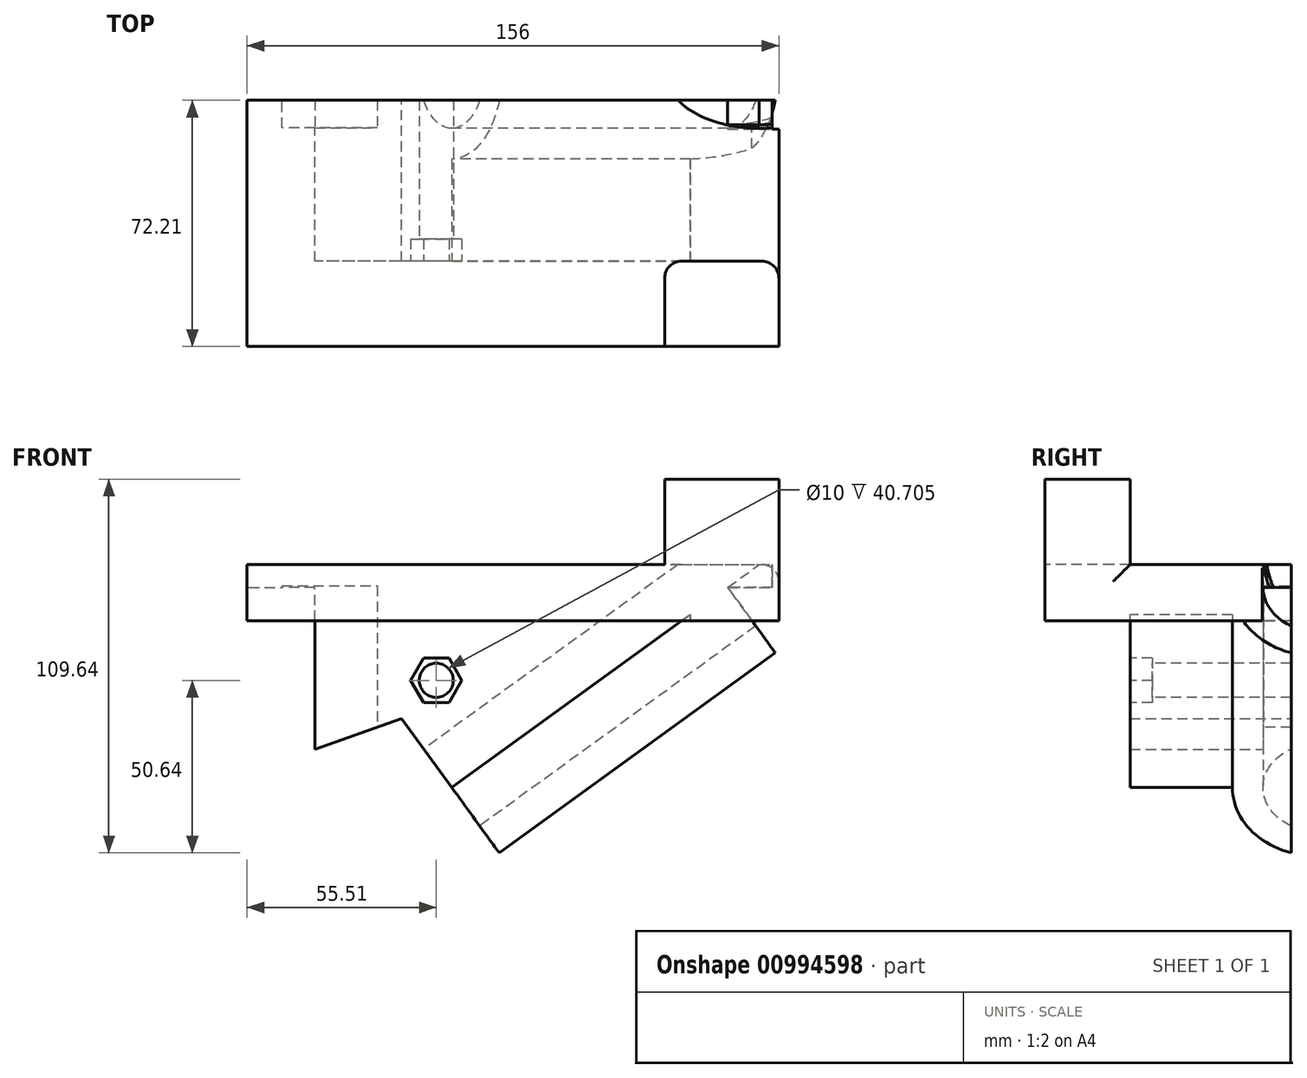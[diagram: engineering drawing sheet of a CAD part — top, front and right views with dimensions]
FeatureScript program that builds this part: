
annotation { "Feature Type Name" : "Feature", "Feature Type Description" : "" }
export const myFeature = defineFeature(function(context is Context, id is Id, definition is map)
    precondition{}
    {
        {
            var Q0;
            Q0=qCreatedBy(makeId("Front.planeOp"),FACE);
            var sketch = newSketch(context, id + "F0", { "sketchPlane" : qUnion([Q0])});
            skLineSegment(sketch, "E0.bottom", {"start": v(65.5, 0) * mm, "end": v(-65.5, 0) * mm});
            skLineSegment(sketch, "E0.top", {"start": v(65.5, 155.25) * mm, "end": v(-65.5, 155.25) * mm});
            skLineSegment(sketch, "E0.left", {"start": v(65.5, 0) * mm, "end": v(65.5, 155.25) * mm});
            skLineSegment(sketch, "E0.right", {"start": v(-65.5, 0) * mm, "end": v(-65.5, 155.25) * mm});
            skLineSegment(sketch, "E1.bottom", {"start": v(-65.5, 0) * mm, "end": v(89.5, 0) * mm});
            skLineSegment(sketch, "E1.top", {"start": v(-65.5, -12.7) * mm, "end": v(89.5, -12.7) * mm});
            skLineSegment(sketch, "E1.left", {"start": v(-65.5, 0) * mm, "end": v(-65.5, -12.7) * mm});
            skLineSegment(sketch, "E1.right", {"start": v(89.5, 0) * mm, "end": v(89.5, -12.7) * mm});
            skCircle(sketch, "E2", {"center": v(-32.75, 57) * mm, "radius": 5 * mm});
            skCircle(sketch, "E3.0.1.0", {"center": v(-32.75, 122.5) * mm, "radius": 5 * mm});
            skCircle(sketch, "E3.1.0.0", {"center": v(32.75, 57) * mm, "radius": 5 * mm});
            skCircle(sketch, "E3.1.1.0", {"center": v(32.75, 122.5) * mm, "radius": 5 * mm});
            skLineSegment(sketch, "E3.direction1", {"start": v(-32.75, 57) * mm, "end": v(32.75, 57) * mm, "construction": true});
            skLineSegment(sketch, "E3.direction2", {"start": v(-32.75, 57) * mm, "end": v(-32.75, 122.5) * mm, "construction": true});
            skCircle(sketch, "E4", {"center": v(0, 89.75) * mm, "radius": 10 * mm});
            skSolve(sketch);
        }
        {
            var Q0;
            Q0=makeQuery(id+"F0.imprint","IMPRINT",FACE,{"disambiguationData":[TD([[makeQuery(id+"F0.imprint","IMPRINT",EDGE,{"derivedFrom":sQuery(id+"F0.wireOp",EDGE,"E0.top")}),1.0]])]});
            extrude(context, id + "F1", {"entities" : qUnion([Q0]), "oppositeDirection" : true, "depth" : 12.7 * mm, "offsetDistance" : 25 * mm});
        }
        {
            var Q0;
            Q0=makeQuery(id+"F0.imprint","IMPRINT",FACE,{"disambiguationData":[TD([[makeQuery(id+"F0.imprint","IMPRINT",EDGE,{"derivedFrom":sQuery(id+"F0.wireOp",EDGE,"E1.bottom")}),-1.0]])]});
            extrude(context, id + "F2", {"entities" : qUnion([Q0]), "operationType" : NewBodyOperationType.ADD, "oppositeDirection" : true, "depth" : 150 * mm, "offsetDistance" : 25 * mm});
        }
        {
            var Q0;
            Q0=makeQuery(id+"F2.opExtrude","SWEPT_FACE",FACE,{"disambiguationData":[OSD([sQuery(id+"F0.wireOp",EDGE,"E1.top")])]});
            var sketch = newSketch(context, id + "F3", { "sketchPlane" : qUnion([Q0])});
            skLineSegment(sketch, "E5", {"start": v(89.5, -12.7) * mm, "end": v(-65.5, -12.7) * mm});
            skCircle(sketch, "E6", {"center": v(-40, -55.7) * mm, "radius": 4.76 * mm});
            skCircle(sketch, "E7.0.1.0", {"center": v(-40, -118.2) * mm, "radius": 4.76 * mm});
            skCircle(sketch, "E7.1.0.0", {"center": v(64, -55.7) * mm, "radius": 4.76 * mm});
            skCircle(sketch, "E7.1.1.0", {"center": v(64, -118.2) * mm, "radius": 4.76 * mm});
            skLineSegment(sketch, "E7.direction1", {"start": v(-40, -55.7) * mm, "end": v(64, -55.7) * mm, "construction": true});
            skLineSegment(sketch, "E7.direction2", {"start": v(-40, -55.7) * mm, "end": v(-40, -118.2) * mm, "construction": true});
            skSolve(sketch);
        }
        {
            var Q0;
            Q0=makeQuery(id+"F3.imprint","IMPRINT",FACE,{"disambiguationData":[TD([[makeQuery(id+"F3.imprint","IMPRINT",EDGE,{"derivedFrom":sQuery(id+"F3.wireOp",EDGE,"E6")}),1.0]])]});
            var Q1;
            Q1=makeQuery(id+"F3.imprint","IMPRINT",FACE,{"disambiguationData":[TD([[makeQuery(id+"F3.imprint","IMPRINT",EDGE,{"derivedFrom":sQuery(id+"F3.wireOp",EDGE,"E7.0.1.0")}),1.0]])]});
            var Q2;
            Q2=makeQuery(id+"F3.imprint","IMPRINT",FACE,{"disambiguationData":[TD([[makeQuery(id+"F3.imprint","IMPRINT",EDGE,{"derivedFrom":sQuery(id+"F3.wireOp",EDGE,"E7.1.1.0")}),1.0]])]});
            var Q3;
            Q3=makeQuery(id+"F3.imprint","IMPRINT",FACE,{"disambiguationData":[TD([[makeQuery(id+"F3.imprint","IMPRINT",EDGE,{"derivedFrom":sQuery(id+"F3.wireOp",EDGE,"E7.1.0.0")}),1.0]])]});
            extrude(context, id + "F4", {"entities" : qUnion([Q0, Q1, Q2, Q3]), "operationType" : NewBodyOperationType.REMOVE, "endBound" : BoundingType.THROUGH_ALL, "oppositeDirection" : true, "depth" : 25 * mm, "offsetDistance" : 25 * mm});
        }
        {
            var Q0;
            {var subQ0=sQuery(id+"F0.wireOp",EDGE,"E1.bottom");Q0=makeQuery(id+"F2.boolean.opBoolean","MERGE",FACE,{"derivedFrom":[makeQuery(id+"F1.opExtrude","CAP_FACE",FACE,{"disambiguationData":[OSD([sQuery(id+"F0.wireOp",EDGE,"E0.top"),sQuery(id+"F0.wireOp",EDGE,"E0.left"),sQuery(id+"F0.wireOp",EDGE,"E0.right"),subQ0,sQuery(id+"F0.wireOp",EDGE,"E2"),sQuery(id+"F0.wireOp",EDGE,"E3.0.1.0"),sQuery(id+"F0.wireOp",EDGE,"E3.1.0.0"),sQuery(id+"F0.wireOp",EDGE,"E3.1.1.0"),sQuery(id+"F0.wireOp",EDGE,"E4")])],"isStart":true}),makeQuery(id+"F2.opExtrude","CAP_FACE",FACE,{"disambiguationData":[OSD([subQ0,sQuery(id+"F0.wireOp",EDGE,"E1.top"),sQuery(id+"F0.wireOp",EDGE,"E1.left"),sQuery(id+"F0.wireOp",EDGE,"E1.right")])],"isStart":true})]});}
            var sketch = newSketch(context, id + "F5", { "sketchPlane" : qUnion([Q0])});
            skLineSegment(sketch, "E8", {"start": v(-63.5, -12.7) * mm, "end": v(-44.93, -100.76) * mm});
            skLineSegment(sketch, "E9", {"start": v(-44.93, -100.76) * mm, "end": v(76.5, -12.7) * mm});
            skSolve(sketch);
        }
        {
            var Q0;
            {var subQ0=sQuery(id+"F5.wireOp",EDGE,"E8");Q0=makeQuery(id+"F5.imprint","IMPRINT",FACE,{"disambiguationData":[TD([[makeQuery(id+"F5.imprint","IMPRINT",EDGE,{"derivedFrom":subQ0}),1.0]])]});}
            extrude(context, id + "F6", {"entities" : qUnion([Q0]), "operationType" : NewBodyOperationType.ADD, "oppositeDirection" : true, "depth" : 55 * mm, "offsetDistance" : 25 * mm});
        }
        {
            var Q0;
            Q0=makeQuery(id+"F6.opExtrude","SWEPT_FACE",FACE,{"disambiguationData":[OSD([sQuery(id+"F5.wireOp",EDGE,"E9")])]});
            var sketch = newSketch(context, id + "F7", { "sketchPlane" : qUnion([Q0])});
            skLineSegment(sketch, "E10", {"start": v(54.47, -55) * mm, "end": v(-45.53, -55) * mm});
            skLineSegment(sketch, "E11", {"start": v(-45.53, -55) * mm, "end": v(-45.53, -30) * mm});
            skLineSegment(sketch, "E12", {"start": v(-45.53, -30) * mm, "end": v(54.47, -30) * mm});
            skLineSegment(sketch, "E13", {"start": v(54.47, -30) * mm, "end": v(54.47, -55) * mm});
            skLineSegment(sketch, "E14", {"start": v(-45.53, -40) * mm, "end": v(18.27, -40) * mm});
            skLineSegment(sketch, "E15", {"start": v(18.27, -40) * mm, "end": v(54.47, -40) * mm});
            skSolve(sketch);
        }
        {
            var Q0;
            {var subQ2=sQuery(id+"F7.wireOp",EDGE,"E12");Q0=makeQuery(id+"F7.imprint","IMPRINT",FACE,{"disambiguationData":[TD([[makeQuery(id+"F7.imprint","IMPRINT",EDGE,{"derivedFrom":subQ2}),-1.0]])]});}
            var Q1;
            Q1=sQuery(id+"F7.wireOp",EDGE,"E10");
            revolve(context, id + "F8", {"operationType" : NewBodyOperationType.ADD, "surfaceOperationType" : NewSurfaceOperationType.NEW, "entities" : qUnion([Q0]), "axis" : qUnion([Q1]), "revolveType" : RevolveType.FULL, "oppositeDirection" : true});
        }
        {
            var Q0;
            Q0=makeQuery(id+"F2.opExtrude","SWEPT_FACE",FACE,{"disambiguationData":[OSD([sQuery(id+"F0.wireOp",EDGE,"E1.right")])]});
            var sketch = newSketch(context, id + "F9", { "sketchPlane" : qUnion([Q0])});
            skLineSegment(sketch, "E16.bottom", {"start": v(34.14, 0) * mm, "end": v(80.6, 0) * mm});
            skLineSegment(sketch, "E16.top", {"start": v(34.14, 23.6) * mm, "end": v(80.6, 23.6) * mm});
            skLineSegment(sketch, "E16.left", {"start": v(34.14, 0) * mm, "end": v(34.14, 23.6) * mm});
            skLineSegment(sketch, "E16.right", {"start": v(80.6, 0) * mm, "end": v(80.6, 23.6) * mm});
            skSolve(sketch);
        }
        {
            var Q0;
            Q0=makeQuery(id+"F9.imprint","IMPRINT",FACE,{"disambiguationData":[TD([[makeQuery(id+"F9.imprint","IMPRINT",EDGE,{"derivedFrom":sQuery(id+"F9.wireOp",EDGE,"E16.bottom")}),-1.0]])]});
            extrude(context, id + "F10", {"entities" : qUnion([Q0]), "operationType" : NewBodyOperationType.REMOVE, "oppositeDirection" : true, "depth" : 100.62 * mm, "offsetDistance" : 25 * mm});
        }
        {
            var Q0;
            Q0=qCreatedBy(makeId("Front.planeOp"),FACE);
            var sketch = newSketch(context, id + "F11", { "sketchPlane" : qUnion([Q0])});
            skLineSegment(sketch, "E17.bottom", {"start": v(-4.59, -72.84) * mm, "end": v(-55.62, -72.84) * mm});
            skLineSegment(sketch, "E17.top", {"start": v(-4.59, -104.11) * mm, "end": v(-55.62, -104.11) * mm});
            skLineSegment(sketch, "E17.left", {"start": v(-4.59, -72.84) * mm, "end": v(-4.59, -104.11) * mm});
            skLineSegment(sketch, "E17.right", {"start": v(-55.62, -72.84) * mm, "end": v(-55.62, -104.11) * mm});
            skLineSegment(sketch, "E18.bottom", {"start": v(-63.9, -12.7) * mm, "end": v(-44.63, -12.7) * mm});
            skLineSegment(sketch, "E18.top", {"start": v(-63.9, -72.84) * mm, "end": v(-44.63, -72.84) * mm});
            skLineSegment(sketch, "E18.left", {"start": v(-63.9, -12.7) * mm, "end": v(-63.9, -72.84) * mm});
            skLineSegment(sketch, "E18.right", {"start": v(-44.63, -12.7) * mm, "end": v(-44.63, -72.84) * mm});
            skSolve(sketch);
        }
        {
            var Q0;
            Q0=makeQuery(id+"F11.imprint","IMPRINT",FACE,{"disambiguationData":[TD([[makeQuery(id+"F11.imprint","IMPRINT",EDGE,{"derivedFrom":sQuery(id+"F11.wireOp",EDGE,"E18.bottom")}),-1.0]])]});
            var Q1;
            {var subQ1=sQuery(id+"F11.wireOp",EDGE,"E17.bottom");Q1=makeQuery(id+"F11.imprint","IMPRINT",FACE,{"disambiguationData":[TD([[makeQuery(id+"F11.imprint","IMPRINT",EDGE,{"derivedFrom":subQ1}),1.0]])]});}
            extrude(context, id + "F12", {"entities" : qUnion([Q0, Q1]), "operationType" : NewBodyOperationType.REMOVE, "endBound" : BoundingType.THROUGH_ALL, "oppositeDirection" : true, "depth" : 63.06 * mm, "offsetDistance" : 25 * mm});
        }
        {
            var Q0;
            Q0=makeQuery(id+"F6.opExtrude","CAP_FACE",FACE,{"disambiguationData":[OSD([sQuery(id+"F0.wireOp",EDGE,"E1.top"),sQuery(id+"F5.wireOp",EDGE,"E8"),sQuery(id+"F5.wireOp",EDGE,"E9")])],"isStart":false});
            var sketch = newSketch(context, id + "F13", { "sketchPlane" : qUnion([Q0])});
            skLineSegment(sketch, "E19", {"start": v(19.13, -51.17) * mm, "end": v(-10.05, -91.4) * mm});
            skLineSegment(sketch, "E20", {"start": v(-10.05, -91.4) * mm, "end": v(37.2, -125.68) * mm});
            skLineSegment(sketch, "E21", {"start": v(37.2, -125.68) * mm, "end": v(76.4, -71.65) * mm});
            skLineSegment(sketch, "E22", {"start": v(76.4, -71.65) * mm, "end": v(19.13, -51.17) * mm});
            skSolve(sketch);
        }
        {
            var Q0;
            {var subQ10=sQuery(id+"F13.wireOp",EDGE,"E20");Q0=makeQuery(id+"F13.imprint","IMPRINT",FACE,{"disambiguationData":[TD([[makeQuery(id+"F13.imprint","IMPRINT",EDGE,{"derivedFrom":subQ10}),1.0]])]});}
            var Q1;
            {var subQ0=sQuery(id+"F5.wireOp",EDGE,"E9");var subQ1=makeQuery(id+"F6.opExtrude","CAP_FACE",FACE,{"disambiguationData":[OSD([sQuery(id+"F0.wireOp",EDGE,"E1.top"),sQuery(id+"F5.wireOp",EDGE,"E8"),subQ0])],"isStart":false});var subQ2=subQ1;var subQ3=makeQuery(id+"F12.boolean.opBoolean","INTERSECT",EDGE,{"derivedFrom":[subQ2,makeQuery(id+"F12.opExtrude","SWEPT_FACE",FACE,{"disambiguationData":[OSD([sQuery(id+"F11.wireOp",EDGE,"E17.bottom")])]})]});Q1=makeQuery(id+"F13.imprint","IMPRINT",FACE,{"disambiguationData":[TD([[makeQuery(id+"F13.imprint","IMPRINT",EDGE,{"derivedFrom":subQ3}),1.0]])]});}
            extrude(context, id + "F14", {"entities" : qUnion([Q0, Q1]), "operationType" : NewBodyOperationType.REMOVE, "oppositeDirection" : true, "depth" : 89 * mm, "offsetDistance" : 25 * mm});
        }
        {
            var Q0;
            Q0=makeQuery(id+"F14.boolean.opBoolean","MERGE",FACE,{"derivedFrom":[makeQuery(id+"F8.opRevolve","SWEPT_FACE",FACE,{"disambiguationData":[OSD([sQuery(id+"F7.wireOp",EDGE,"E11")])]})],"fromTools":[makeQuery(id+"F14.opExtrude","SWEPT_FACE",FACE,{"disambiguationData":[OSD([sQuery(id+"F13.wireOp",EDGE,"E19")])]})]});
            var sketch = newSketch(context, id + "F15", { "sketchPlane" : qUnion([Q0])});
            skCircle(sketch, "E23", {"center": v(-55, -55.2) * mm, "radius": 16 * mm});
            skSolve(sketch);
        }
        {
            var Q0;
            {var subQ0=sQuery(id+"F13.wireOp",EDGE,"E19");Q0=makeQuery(id+"F15.imprint","IMPRINT",FACE,{"disambiguationData":[TD([[makeQuery(id+"F15.imprint","IMPRINT",EDGE,{"derivedFrom":makeQuery(id+"F14.boolean.opBoolean","COPY",EDGE,{"derivedFrom":makeQuery(id+"F14.opExtrude","CAP_EDGE",EDGE,{"disambiguationData":[OSD([subQ0])],"isStart":true})})}),-1.0]])]});}
            var Q1;
            Q1=makeQuery(id+"F15.imprint","IMPRINT",FACE,{"disambiguationData":[TD([[makeQuery(id+"F15.imprint","IMPRINT",EDGE,{"derivedFrom":sQuery(id+"F15.wireOp",EDGE,"E23")}),1.0]])]});
            extrude(context, id + "F16", {"entities" : qUnion([Q0, Q1]), "operationType" : NewBodyOperationType.REMOVE, "endBound" : BoundingType.THROUGH_ALL, "oppositeDirection" : true, "depth" : 25 * mm, "offsetDistance" : 25 * mm});
        }
        {
            var Q0;
            {var subQ1=sQuery(id+"F0.wireOp",EDGE,"E1.right");var subQ3=sQuery(id+"F0.wireOp",EDGE,"E1.top");var subQ6=makeQuery(id+"F2.opExtrude","SWEPT_FACE",FACE,{"disambiguationData":[OSD([subQ3])]});var subQ14=makeQuery(id+"F2.opExtrude","SWEPT_FACE",FACE,{"disambiguationData":[OSD([subQ1])]});var subQ17=makeQuery(id+"F4.boolean.opBoolean","COPY",FACE,{"derivedFrom":makeQuery(id+"F4.opExtrude","SWEPT_FACE",FACE,{"disambiguationData":[OSD([sQuery(id+"F3.wireOp",EDGE,"E6")])]})});Q0=makeQuery(id+"F16.boolean.opBoolean","SPLIT",FACE,{"disambiguationData":[TD([subQ17])],"derivedFrom":makeQuery(id+"F12.boolean.opBoolean","SPLIT",FACE,{"disambiguationData":[TD([subQ14])],"derivedFrom":subQ6})});}
            cPlane(context, id + "F17", {"entities" : qUnion([Q0]), "cplaneType" : CPlaneType.OFFSET, "offset" : 57.01 * mm, "width" : 150 * mm, "height" : 150 * mm});
        }
        {
            var Q0;
            Q0=qCreatedBy(id+"F17.planeOp",FACE);
            var sketch = newSketch(context, id + "F18", { "sketchPlane" : qUnion([Q0])});
            skLineSegment(sketch, "E24.bottom", {"start": v(-26.24, -39.17) * mm, "end": v(-54.25, -39.17) * mm});
            skLineSegment(sketch, "E24.top", {"start": v(-26.24, -72.55) * mm, "end": v(-54.25, -72.55) * mm});
            skLineSegment(sketch, "E24.left", {"start": v(-26.24, -39.17) * mm, "end": v(-26.24, -72.55) * mm});
            skLineSegment(sketch, "E24.right", {"start": v(-54.25, -39.17) * mm, "end": v(-54.25, -72.55) * mm});
            skSolve(sketch);
        }
        {
            var Q0;
            Q0=makeQuery(id+"F18.imprint","IMPRINT",FACE,{"disambiguationData":[TD([[makeQuery(id+"F18.imprint","IMPRINT",EDGE,{"derivedFrom":sQuery(id+"F18.wireOp",EDGE,"E24.bottom")}),1.0]])]});
            extrude(context, id + "F19", {"entities" : qUnion([Q0]), "operationType" : NewBodyOperationType.REMOVE, "oppositeDirection" : true, "depth" : 57.44 * mm, "offsetDistance" : 25 * mm});
        }
        {
            var Q0;
            {var subQ1=sQuery(id+"F0.wireOp",EDGE,"E1.right");var subQ3=sQuery(id+"F0.wireOp",EDGE,"E1.top");var subQ6=makeQuery(id+"F2.opExtrude","SWEPT_FACE",FACE,{"disambiguationData":[OSD([subQ3])]});var subQ14=makeQuery(id+"F2.opExtrude","SWEPT_FACE",FACE,{"disambiguationData":[OSD([subQ1])]});var subQ17=makeQuery(id+"F4.boolean.opBoolean","COPY",FACE,{"derivedFrom":makeQuery(id+"F4.opExtrude","SWEPT_FACE",FACE,{"disambiguationData":[OSD([sQuery(id+"F3.wireOp",EDGE,"E6")])]})});Q0=makeQuery(id+"F16.boolean.opBoolean","SPLIT",FACE,{"disambiguationData":[TD([subQ17])],"derivedFrom":makeQuery(id+"F12.boolean.opBoolean","SPLIT",FACE,{"disambiguationData":[TD([subQ14])],"derivedFrom":subQ6})});}
            cPlane(context, id + "F20", {"entities" : qUnion([Q0]), "cplaneType" : CPlaneType.OFFSET, "offset" : 94.9 * mm, "width" : 150 * mm, "height" : 150 * mm});
        }
        {
            var Q0;
            Q0=makeQuery(id+"F2.opExtrude","CAP_FACE",FACE,{"disambiguationData":[OSD([sQuery(id+"F0.wireOp",EDGE,"E1.bottom"),sQuery(id+"F0.wireOp",EDGE,"E1.top"),sQuery(id+"F0.wireOp",EDGE,"E1.left"),sQuery(id+"F0.wireOp",EDGE,"E1.right")])],"isStart":false});
            cPlane(context, id + "F21", {"entities" : qUnion([Q0]), "cplaneType" : CPlaneType.OFFSET, "offset" : 83.64 * mm, "oppositeDirection" : true, "width" : 150 * mm, "height" : 150 * mm});
        }
        {
            var Q0;
            Q0=qCreatedBy(id+"F21.planeOp",FACE);
            var sketch = newSketch(context, id + "F22", { "sketchPlane" : qUnion([Q0])});
            skLineSegment(sketch, "E25.bottom", {"start": v(-19.5, -47.14) * mm, "end": v(25.5, -47.14) * mm});
            skLineSegment(sketch, "E25.top", {"start": v(-19.5, -10.84) * mm, "end": v(25.5, -10.84) * mm});
            skLineSegment(sketch, "E25.left", {"start": v(-19.5, -47.14) * mm, "end": v(-19.5, -10.84) * mm});
            skLineSegment(sketch, "E25.right", {"start": v(25.5, -47.14) * mm, "end": v(25.5, -10.84) * mm});
            skLineSegment(sketch, "E26", {"start": v(9.29, -47.14) * mm, "end": v(-19.5, -25.37) * mm});
            skSolve(sketch);
        }
        {
            var Q0;
            {var subQ2=sQuery(id+"F22.wireOp",EDGE,"E25.top");Q0=makeQuery(id+"F22.imprint","IMPRINT",FACE,{"disambiguationData":[TD([[makeQuery(id+"F22.imprint","IMPRINT",EDGE,{"derivedFrom":subQ2}),-1.0]])]});}
            extrude(context, id + "F23", {"entities" : qUnion([Q0]), "operationType" : NewBodyOperationType.ADD, "oppositeDirection" : true, "depth" : 37.3 * mm, "offsetDistance" : 25 * mm});
        }
        {
            var Q0;
            Q0=qCreatedBy(id+"F20.planeOp",FACE);
            var sketch = newSketch(context, id + "F24", { "sketchPlane" : qUnion([Q0])});
            skLineSegment(sketch, "E27", {"start": v(-70.25, -47.2) * mm, "end": v(105.05, -47.2) * mm});
            skLineSegment(sketch, "E28", {"start": v(105.05, -47.2) * mm, "end": v(105.05, 16.74) * mm});
            skLineSegment(sketch, "E29", {"start": v(105.05, 16.74) * mm, "end": v(-70.14, 16.74) * mm});
            skLineSegment(sketch, "E30", {"start": v(-70.14, 16.74) * mm, "end": v(-70.25, -47.2) * mm});
            skLineSegment(sketch, "E31", {"start": v(-70.25, -47.2) * mm, "end": v(-70.25, -164.49) * mm});
            skLineSegment(sketch, "E32", {"start": v(-70.25, -164.49) * mm, "end": v(108.53, -164.49) * mm});
            skLineSegment(sketch, "E33", {"start": v(108.53, -164.49) * mm, "end": v(105.05, -47.2) * mm});
            skSolve(sketch);
        }
        {
            var Q0;
            Q0=makeQuery(id+"F24.imprint","IMPRINT",FACE,{"disambiguationData":[TD([[makeQuery(id+"F24.imprint","IMPRINT",EDGE,{"derivedFrom":sQuery(id+"F24.wireOp",EDGE,"E27")}),-1.0]])]});
            extrude(context, id + "F25", {"entities" : qUnion([Q0]), "operationType" : NewBodyOperationType.REMOVE, "endBound" : BoundingType.THROUGH_ALL, "oppositeDirection" : true, "depth" : 25 * mm, "offsetDistance" : 25 * mm});
        }
        {
            var Q0;
            Q0=qCreatedBy(makeId("Front.planeOp"),FACE);
            var sketch = newSketch(context, id + "F26", { "sketchPlane" : qUnion([Q0])});
            skLineSegment(sketch, "E34.bottom", {"start": v(65.5, 10.5) * mm, "end": v(-64.5, 10.5) * mm});
            skLineSegment(sketch, "E34.top", {"start": v(65.5, -22.5) * mm, "end": v(-64.5, -22.5) * mm});
            skLineSegment(sketch, "E34.left", {"start": v(65.5, 10.5) * mm, "end": v(65.5, -22.5) * mm});
            skLineSegment(sketch, "E34.right", {"start": v(-64.5, 10.5) * mm, "end": v(-64.5, -22.5) * mm});
            skSolve(sketch);
        }
        {
            var Q0;
            Q0=makeQuery(id+"F26.imprint","IMPRINT",FACE,{"disambiguationData":[TD([[makeQuery(id+"F26.imprint","IMPRINT",EDGE,{"derivedFrom":sQuery(id+"F26.wireOp",EDGE,"E34.bottom")}),1.0]])]});
            extrude(context, id + "F27", {"entities" : qUnion([Q0]), "operationType" : NewBodyOperationType.ADD, "depth" : 25 * mm, "offsetDistance" : 25 * mm});
        }
        {
            var Q0;
            {var subQ2=sQuery(id+"F0.wireOp",EDGE,"E1.top");var subQ8=sQuery(id+"F26.wireOp",EDGE,"E34.top");var subQ9=sQuery(id+"F26.wireOp",EDGE,"E34.right");Q0=makeQuery(id+"F27.boolean.opBoolean","SPLIT",FACE,{"disambiguationData":[TD([makeQuery(id+"F2.opExtrude","SWEPT_FACE",FACE,{"disambiguationData":[OSD([subQ2])]})])],"derivedFrom":makeQuery(id+"F27.opExtrude","CAP_FACE",FACE,{"disambiguationData":[OSD([sQuery(id+"F26.wireOp",EDGE,"E34.bottom"),subQ8,sQuery(id+"F26.wireOp",EDGE,"E34.left"),subQ9])],"isStart":true})});}
            extrude(context, id + "F28", {"entities" : qUnion([Q0]), "operationType" : NewBodyOperationType.ADD, "depth" : 47.17 * mm, "offsetDistance" : 25 * mm});
        }
        {
            var Q0;
            Q0=makeQuery(id+"F27.opExtrude","CAP_FACE",FACE,{"disambiguationData":[OSD([sQuery(id+"F26.wireOp",EDGE,"E34.bottom"),sQuery(id+"F26.wireOp",EDGE,"E34.top"),sQuery(id+"F26.wireOp",EDGE,"E34.left"),sQuery(id+"F26.wireOp",EDGE,"E34.right")])],"isStart":false});
            var sketch = newSketch(context, id + "F29", { "sketchPlane" : qUnion([Q0])});
            skLineSegment(sketch, "E35", {"start": v(102.44, -6) * mm, "end": v(-95.08, -6) * mm});
            skLineSegment(sketch, "E36", {"start": v(102.44, -6) * mm, "end": v(102.44, -90.83) * mm});
            skLineSegment(sketch, "E37", {"start": v(102.44, -90.83) * mm, "end": v(-96.5, -90.83) * mm});
            skLineSegment(sketch, "E38", {"start": v(-96.5, -90.83) * mm, "end": v(-95.08, -6) * mm});
            skLineSegment(sketch, "E39", {"start": v(-95.08, -6) * mm, "end": v(-95.08, 171.2) * mm});
            skLineSegment(sketch, "E40", {"start": v(-95.08, 171.2) * mm, "end": v(114.36, 171.2) * mm});
            skLineSegment(sketch, "E41", {"start": v(114.36, 171.2) * mm, "end": v(102.44, -6) * mm});
            skSolve(sketch);
        }
        {
            var Q0;
            {var subQ0=sQuery(id+"F29.wireOp",EDGE,"E39");Q0=makeQuery(id+"F29.imprint","IMPRINT",FACE,{"disambiguationData":[TD([[makeQuery(id+"F29.imprint","IMPRINT",EDGE,{"derivedFrom":subQ0}),-1.0]])]});}
            var Q1;
            {var subQ5=makeQuery(id+"F27.opExtrude","CAP_EDGE",EDGE,{"disambiguationData":[OSD([sQuery(id+"F26.wireOp",EDGE,"E34.bottom")])],"isStart":false});Q1=makeQuery(id+"F29.imprint","IMPRINT",FACE,{"disambiguationData":[TD([[makeQuery(id+"F29.imprint","IMPRINT",EDGE,{"derivedFrom":subQ5}),1.0]])]});}
            extrude(context, id + "F30", {"entities" : qUnion([Q0, Q1]), "operationType" : NewBodyOperationType.REMOVE, "oppositeDirection" : true, "depth" : 118.07 * mm, "offsetDistance" : 25 * mm});
        }
        {
            var Q0;
            {var subQ0=sQuery(id+"F5.wireOp",EDGE,"E9");var subQ1=sQuery(id+"F5.wireOp",EDGE,"E8");var subQ2=sQuery(id+"F0.wireOp",EDGE,"E1.top");var subQ3=makeQuery(id+"F6.opExtrude","CAP_FACE",FACE,{"disambiguationData":[OSD([subQ2,subQ1,subQ0])],"isStart":true});var subQ4=sQuery(id+"F0.wireOp",EDGE,"E1.bottom");var subQ5=makeQuery(id+"F2.opExtrude","CAP_FACE",FACE,{"disambiguationData":[OSD([subQ4,subQ2,sQuery(id+"F0.wireOp",EDGE,"E1.left"),sQuery(id+"F0.wireOp",EDGE,"E1.right")])],"isStart":true});var subQ6=makeQuery(id+"F1.opExtrude","CAP_FACE",FACE,{"disambiguationData":[OSD([sQuery(id+"F0.wireOp",EDGE,"E0.top"),sQuery(id+"F0.wireOp",EDGE,"E0.left"),sQuery(id+"F0.wireOp",EDGE,"E0.right"),subQ4,sQuery(id+"F0.wireOp",EDGE,"E2"),sQuery(id+"F0.wireOp",EDGE,"E3.0.1.0"),sQuery(id+"F0.wireOp",EDGE,"E3.1.0.0"),sQuery(id+"F0.wireOp",EDGE,"E3.1.1.0"),sQuery(id+"F0.wireOp",EDGE,"E4")])],"isStart":true});Q0=makeQuery(id+"F27.boolean.opBoolean","SPLIT",FACE,{"disambiguationData":[TD([makeQuery(id+"F8.opRevolve","SWEPT_FACE",FACE,{"disambiguationData":[OSD([sQuery(id+"F7.wireOp",EDGE,"E11")])]})])],"derivedFrom":makeQuery(id+"F6.boolean.opBoolean","MERGE",FACE,{"derivedFrom":[makeQuery(id+"F2.boolean.opBoolean","MERGE",FACE,{"derivedFrom":[subQ6,subQ5]}),subQ3]})});}
            var sketch = newSketch(context, id + "F31", { "sketchPlane" : qUnion([Q0])});
            skCircle(sketch, "E42.cCircle", {"center": v(-9, -40) * mm, "radius": 6.5 * mm, "construction": true});
            skLineSegment(sketch, "E42.0", {"start": v(-5.25, -46.5) * mm, "end": v(-12.75, -46.5) * mm});
            skLineSegment(sketch, "E42.1", {"start": v(-12.75, -46.5) * mm, "end": v(-16.5, -40) * mm});
            skLineSegment(sketch, "E42.2", {"start": v(-16.5, -40) * mm, "end": v(-12.75, -33.5) * mm});
            skLineSegment(sketch, "E42.3", {"start": v(-12.75, -33.5) * mm, "end": v(-5.25, -33.5) * mm});
            skLineSegment(sketch, "E42.4", {"start": v(-5.25, -33.5) * mm, "end": v(-1.5, -40) * mm});
            skLineSegment(sketch, "E42.5", {"start": v(-1.5, -40) * mm, "end": v(-5.25, -46.5) * mm});
            skPoint(sketch, "E42.0.midPoint", {"position": v(-9, -46.5) * mm});
            skSolve(sketch);
        }
        {
            var Q0;
            Q0=makeQuery(id+"F31.imprint","IMPRINT",FACE,{"disambiguationData":[TD([[makeQuery(id+"F31.imprint","IMPRINT",EDGE,{"derivedFrom":sQuery(id+"F31.wireOp",EDGE,"E42.0")}),-1.0]])]});
            extrude(context, id + "F32", {"entities" : qUnion([Q0]), "operationType" : NewBodyOperationType.REMOVE, "oppositeDirection" : true, "depth" : 6.5 * mm, "offsetDistance" : 25 * mm});
        }
        {
            var Q0;
            Q0=makeQuery(id+"F31.imprint","IMPRINT",FACE,{"disambiguationData":[TD([[makeQuery(id+"F31.imprint","IMPRINT",EDGE,{"derivedFrom":sQuery(id+"F31.wireOp",EDGE,"E42.0")}),1.0]])]});
            var sketch = newSketch(context, id + "F33", { "sketchPlane" : qUnion([Q0])});
            skCircle(sketch, "E43", {"center": v(-9, -40) * mm, "radius": 5 * mm});
            skSolve(sketch);
        }
        {
            var Q0;
            Q0=makeQuery(id+"F33.imprint","IMPRINT",FACE,{"disambiguationData":[TD([[makeQuery(id+"F33.imprint","IMPRINT",EDGE,{"derivedFrom":sQuery(id+"F33.wireOp",EDGE,"E43")}),1.0]])]});
            extrude(context, id + "F34", {"entities" : qUnion([Q0]), "operationType" : NewBodyOperationType.REMOVE, "endBound" : BoundingType.THROUGH_ALL, "oppositeDirection" : true, "depth" : 47 * mm, "offsetDistance" : 25 * mm});
        }
        {
            var Q0;
            Q0=makeQuery(id+"F27.opExtrude","SWEPT_FACE",FACE,{"disambiguationData":[OSD([sQuery(id+"F26.wireOp",EDGE,"E34.left")])]});
            var sketch = newSketch(context, id + "F35", { "sketchPlane" : qUnion([Q0])});
            skLineSegment(sketch, "E44.bottom", {"start": v(-25, -6) * mm, "end": v(38.73, -6) * mm});
            skLineSegment(sketch, "E44.top", {"start": v(-25, -22.5) * mm, "end": v(38.73, -22.5) * mm});
            skLineSegment(sketch, "E44.left", {"start": v(-25, -6) * mm, "end": v(-25, -22.5) * mm});
            skLineSegment(sketch, "E44.right", {"start": v(38.73, -6) * mm, "end": v(38.73, -22.5) * mm});
            skSolve(sketch);
        }
        {
            var Q0;
            Q0 = qSketchRegion(id + "F35", true);
            extrude(context, id + "F36", {"entities" : qUnion([Q0]), "operationType" : NewBodyOperationType.ADD, "depth" : 26 * mm, "offsetDistance" : 25 * mm});
        }
        {
            var Q0;
            Q0=makeQuery(id+"F30.boolean.opBoolean","COPY",FACE,{"derivedFrom":makeQuery(id+"F30.opExtrude","SWEPT_FACE",FACE,{"disambiguationData":[OSD([sQuery(id+"F29.wireOp",EDGE,"E35")])]})});
            var sketch = newSketch(context, id + "F37", { "sketchPlane" : qUnion([Q0])});
            skLineSegment(sketch, "E45.bottom", {"start": v(58, 0) * mm, "end": v(91.5, 0) * mm});
            skLineSegment(sketch, "E45.top", {"start": v(58, -25) * mm, "end": v(91.5, -25) * mm});
            skLineSegment(sketch, "E45.left", {"start": v(58, 0) * mm, "end": v(58, -25) * mm});
            skLineSegment(sketch, "E45.right", {"start": v(91.5, 0) * mm, "end": v(91.5, -25) * mm});
            skSolve(sketch);
        }
        {
            var Q0;
            Q0=makeQuery(id+"F37.imprint","IMPRINT",FACE,{"disambiguationData":[TD([[makeQuery(id+"F37.imprint","IMPRINT",EDGE,{"derivedFrom":sQuery(id+"F37.wireOp",EDGE,"E45.bottom")}),-1.0]])]});
            extrude(context, id + "F38", {"entities" : qUnion([Q0]), "operationType" : NewBodyOperationType.ADD, "depth" : 25 * mm, "offsetDistance" : 25 * mm});
        }
        {
            var Q0;
            Q0=makeQuery(id+"F38.opExtrude","SWEPT_EDGE",EDGE,{"disambiguationData":[OSD([sQuery(id+"F37.wireOp",EDGE,"E45.bottom"),sQuery(id+"F37.wireOp",EDGE,"E45.left")])]});
            var Q1;
            Q1=makeQuery(id+"F38.opExtrude","SWEPT_EDGE",EDGE,{"disambiguationData":[OSD([sQuery(id+"F35.wireOp",EDGE,"E44.bottom"),sQuery(id+"F37.wireOp",EDGE,"E45.bottom"),sQuery(id+"F37.wireOp",EDGE,"E45.right")])]});
            var Q2;
            Q2=makeQuery(id+"F36.opExtrude","CAP_EDGE",EDGE,{"disambiguationData":[OSD([sQuery(id+"F35.wireOp",EDGE,"E44.bottom")])],"isStart":false});
            fillet(context, id + "F39", {"entities" : qUnion([Q0, Q1, Q2]), "radius" : 5 * mm, "tangentPropagation" : true, "allowEdgeOverflow" : false});
        }
        {
            var Q0;
            {var subQ0=sQuery(id+"F26.wireOp",EDGE,"E34.top");Q0=makeQuery(id+"F36.boolean.opBoolean","MERGE",FACE,{"derivedFrom":[makeQuery(id+"F28.boolean.opBoolean","MERGE",FACE,{"derivedFrom":[makeQuery(id+"F27.opExtrude","SWEPT_FACE",FACE,{"disambiguationData":[OSD([subQ0])]}),makeQuery(id+"F28.opExtrude","SWEPT_FACE",FACE,{"disambiguationData":[OSD([subQ0])]})]}),makeQuery(id+"F36.opExtrude","SWEPT_FACE",FACE,{"disambiguationData":[OSD([sQuery(id+"F35.wireOp",EDGE,"E44.top")])]})]});}
            var sketch = newSketch(context, id + "F40", { "sketchPlane" : qUnion([Q0])});
            skLineSegment(sketch, "E46.bottom", {"start": v(-64.5, 25) * mm, "end": v(-82.23, 25) * mm});
            skLineSegment(sketch, "E46.top", {"start": v(-64.5, -50.18) * mm, "end": v(-82.23, -50.18) * mm});
            skLineSegment(sketch, "E46.left", {"start": v(-64.5, 25) * mm, "end": v(-64.5, -50.18) * mm});
            skLineSegment(sketch, "E46.right", {"start": v(-82.23, 25) * mm, "end": v(-82.23, -50.18) * mm});
            skSolve(sketch);
        }
        {
            var Q0;
            {var subQ4=sQuery(id+"F40.wireOp",EDGE,"E46.bottom");Q0=makeQuery(id+"F40.imprint","IMPRINT",FACE,{"disambiguationData":[TD([[makeQuery(id+"F40.imprint","IMPRINT",EDGE,{"derivedFrom":subQ4}),1.0]])]});}
            extrude(context, id + "F41", {"entities" : qUnion([Q0]), "operationType" : NewBodyOperationType.REMOVE, "oppositeDirection" : true, "depth" : 150.84 * mm, "offsetDistance" : 25 * mm});
        }
    });
